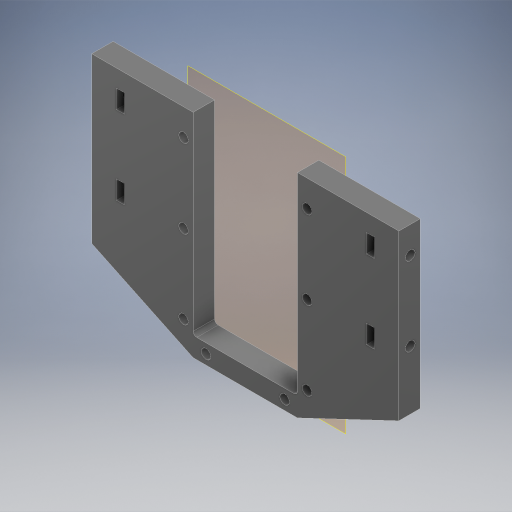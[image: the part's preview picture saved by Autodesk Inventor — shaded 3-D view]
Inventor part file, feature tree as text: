
AUTODESK INVENTOR PART (.ipt)
format: ipt  version: 2024 (Build 280153000, 153)  size: 423,936 bytes
history: native  units: in
note: dims shown in document units (in); Inventor stores cm internally (conversion verified against a paired STEP export)
features: reference x9, other x6, extrude x6, sketch x6, projected_geometry x2, fillet x1, mirror x1
ambient origin geometry x8: Origin, YZ Plane, XZ Plane, XY Plane, X Axis, Y Axis, Z Axis, Center Point
bodies: Body1 (feature_tree)
feature tree (31):
  other  "솔리드2"
  other  "작업 평면1"
  extrude  "돌출4"  Depth=0.0039in
  extrude  "돌출5"  Depth=0.9843in
  extrude  "돌출6"  Depth=2.0866in
  extrude  "돌출7"  Depth=0.1063in
  extrude  "돌출8"  Depth=0.1063in
  fillet  "모깎기5"  Radius=0.1181in
  extrude  "돌출12"  Depth=0.2362in
  mirror  "미러2"
  sketch  "스케치1"
  reference  "참조1"
  reference  "참조2"
  reference  "참조3"
  reference  "참조4"
  reference  "참조5"
  reference  "참조6"
  reference  "참조7"
  reference  "참조8"
  sketch  "스케치3"
  reference  "참조12"
  sketch  "스케치4"
  sketch  "스케치5"
  projected_geometry  "투영된 루프1"
  sketch  "스케치7"
  sketch  "스케치8"
  projected_geometry  "투영된 루프2"
  other  "조립품2"
  other  "MX-64T+idle.ipt:3"
  other  "MX-64T:1"
  other  "MX-64T+idle.ipt:4"
